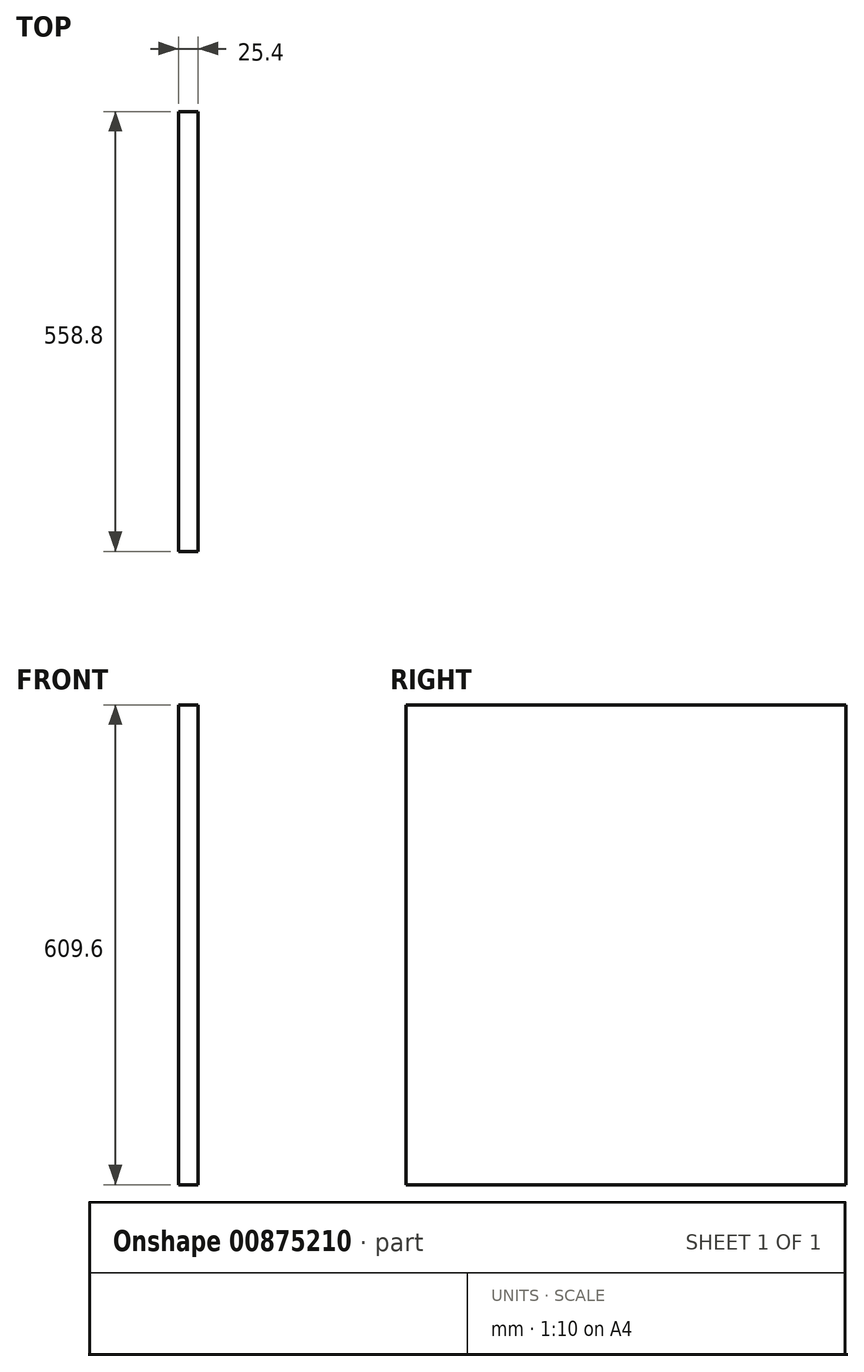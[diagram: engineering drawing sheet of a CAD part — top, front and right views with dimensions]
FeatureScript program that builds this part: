
annotation { "Feature Type Name" : "Feature", "Feature Type Description" : "" }
export const myFeature = defineFeature(function(context is Context, id is Id, definition is map)
    precondition{}
    {
        {
            var Q0;
            Q0=qCreatedBy(makeId("Right.planeOp"),FACE);
            var sketch = newSketch(context, id + "F0", { "sketchPlane" : qUnion([Q0])});
            skLineSegment(sketch, "E0.bottom", {"start": v(-279.4, 304.8) * mm, "end": v(279.4, 304.8) * mm});
            skLineSegment(sketch, "E0.top", {"start": v(-279.4, -304.8) * mm, "end": v(279.4, -304.8) * mm});
            skLineSegment(sketch, "E0.left", {"start": v(-279.4, 304.8) * mm, "end": v(-279.4, -304.8) * mm});
            skLineSegment(sketch, "E0.right", {"start": v(279.4, 304.8) * mm, "end": v(279.4, -304.8) * mm});
            skPoint(sketch, "E0.middle", {"position": v(0, 0) * mm});
            skSolve(sketch);
        }
        {
            var Q0;
            Q0=makeQuery(id+"F0.imprint","IMPRINT",FACE,{"disambiguationData":[TD([[makeQuery(id+"F0.imprint","IMPRINT",EDGE,{"derivedFrom":sQuery(id+"F0.wireOp",EDGE,"E0.bottom")}),-1.0]])]});
            extrude(context, id + "F1", {"entities" : qUnion([Q0]), "depth" : 25.4 * mm, "offsetDistance" : 25.4 * mm});
        }
    });
